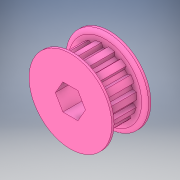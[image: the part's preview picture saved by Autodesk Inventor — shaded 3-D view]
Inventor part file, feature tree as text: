
AUTODESK INVENTOR PART (.ipt)
format: ipt  version: 2017 SP1 (Build 210196100, 196)  size: 237,056 bytes
history: native  units: in
note: dims shown in document units (in); Inventor stores cm internally (conversion verified against a paired STEP export)
features: extrude x2, sketch x2, projected_geometry x1, pattern_circular x1
ambient origin geometry x8: Origin, YZ Plane, XZ Plane, XY Plane, X Axis, Y Axis, Z Axis, Center Point
bodies: Solid1 (feature_tree)
feature tree (6):
  extrude  "Extrusion1"  Depth=1.0in TaperAngle=0.0deg
  extrude  "Extrusion2"  [1 undecoded]
  sketch  "Sketch1"  dims[d0=0.375in d1=1.0in d2=0.0in]
  sketch  "Sketch2"  dims[d3=1.0in d4=0.0in]
  projected_geometry  "Projected Loop1"
  pattern_circular  "CirPattern2"
note: 1 required parameter value undecoded (feature->parameter linkage not recoverable at this tier; creation-order binding heuristic only, values carry confidence <= 0.55)
